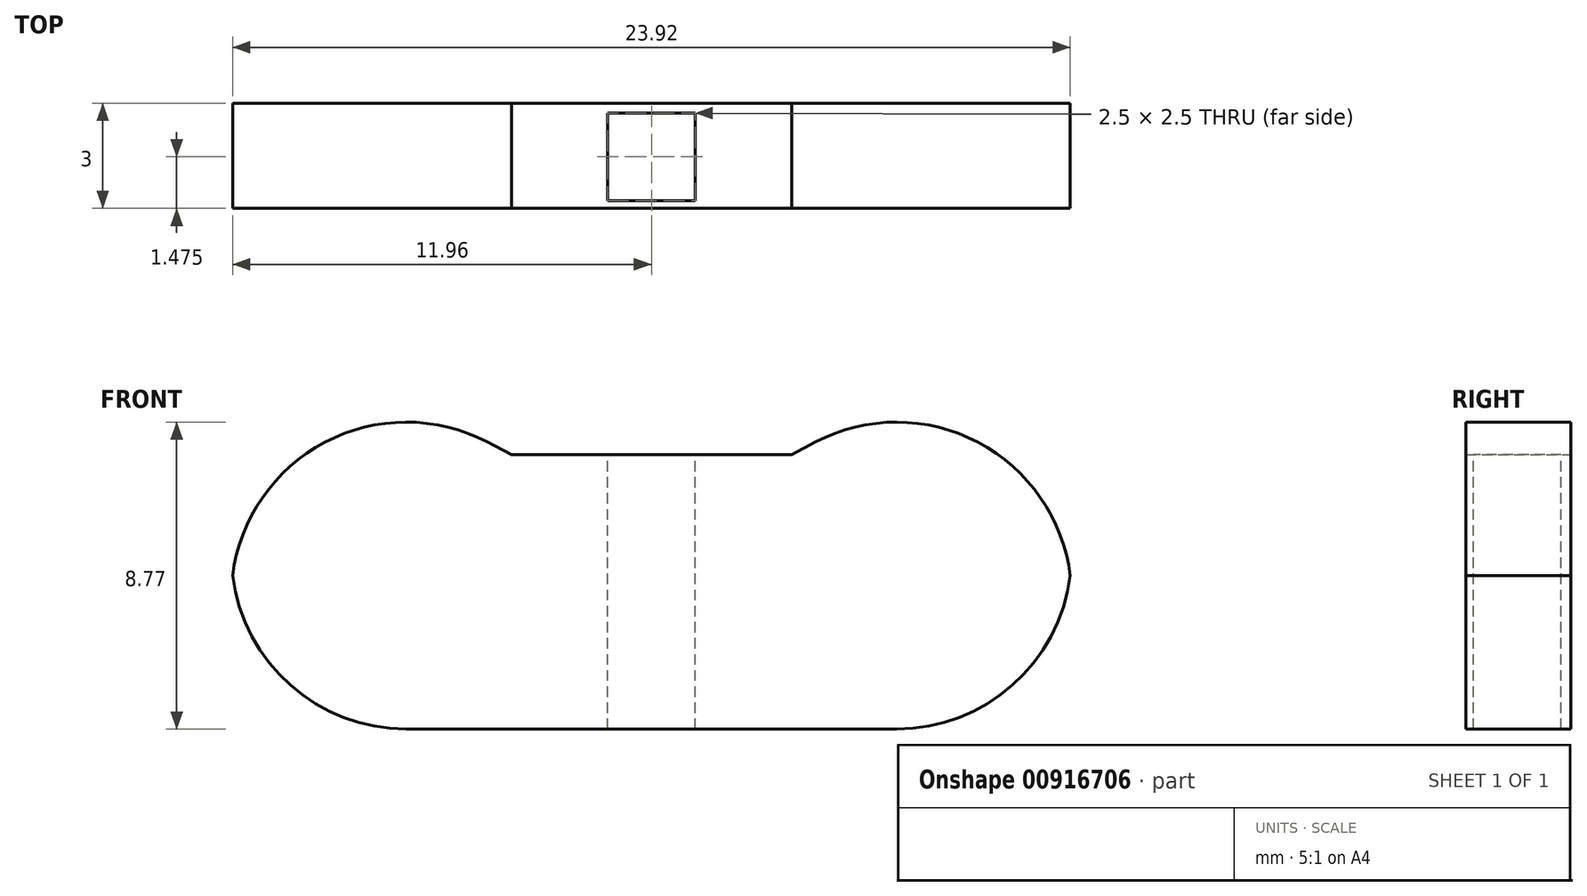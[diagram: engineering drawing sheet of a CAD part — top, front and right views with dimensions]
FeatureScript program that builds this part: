
annotation { "Feature Type Name" : "Feature", "Feature Type Description" : "" }
export const myFeature = defineFeature(function(context is Context, id is Id, definition is map)
    precondition{}
    {
        {
            var Q0;
            Q0=qCreatedBy(makeId("Front.planeOp"),FACE);
            var sketch = newSketch(context, id + "F0", { "sketchPlane" : qUnion([Q0])});
            skLineSegment(sketch, "E0", {"start": v(0, 0) * mm, "end": v(-12, 0) * mm});
            skLineSegment(sketch, "E1", {"start": v(-12, 0) * mm, "end": v(-12, 12) * mm});
            skLineSegment(sketch, "E2", {"start": v(12, 12) * mm, "end": v(12, 0) * mm});
            skLineSegment(sketch, "E3", {"start": v(12, 0) * mm, "end": v(0, 0) * mm});
            skLineSegment(sketch, "E4", {"start": v(0, 7.84) * mm, "end": v(4, 7.84) * mm});
            skLineSegment(sketch, "E5", {"start": v(4, 7.84) * mm, "end": v(0, 7.84) * mm});
            skLineSegment(sketch, "E6", {"start": v(-4, 7.84) * mm, "end": v(0, 7.84) * mm});
            skLineSegment(sketch, "E7", {"start": v(-12, 12) * mm, "end": v(-4, 7.84) * mm});
            skLineSegment(sketch, "E8", {"start": v(4, 7.84) * mm, "end": v(12, 12) * mm});
            skSolve(sketch);
        }
        {
            var Q0;
            Q0=qCreatedBy(makeId("Top.planeOp"),FACE);
            var sketch = newSketch(context, id + "F1", { "sketchPlane" : qUnion([Q0])});
            skLineSegment(sketch, "E9", {"start": v(0, 0) * mm, "end": v(0, 3) * mm});
            skSolve(sketch);
        }
        {
            var Q0;
            Q0 = qSketchRegion(id + "F0", true);
            var Q1;
            Q1 = qConstructionFilter(qBodyType(qCreatedBy(id + "F1" ,EDGE), BodyType.WIRE), ConstructionObject.NO);
            sweep(context, id + "F2", {"profiles" : qUnion([Q0]), "path" : qUnion([Q1])});
        }
        {
            var Q0;
            Q0=makeQuery(id+"F2.opSweep","SWEPT_EDGE",EDGE,{"disambiguationData":[OSD([sQuery(id+"F0.wireOp",EDGE,"RvSbD9WY-HRrn-z7GH-15Zz-RYbIcrGVxp82"),sQuery(id+"F0.wireOp",EDGE,"E2"),sQuery(id+"F1.wireOp",EDGE,"E9")])]});
            fillet(context, id + "F3", {"entities" : qUnion([Q0]), "radius" : 5 * mm, "tangentPropagation" : true, "allowEdgeOverflow" : false});
        }
        {
            var Q0;
            Q0=makeQuery(id+"F2.opSweep","SWEPT_EDGE",EDGE,{"disambiguationData":[OSD([sQuery(id+"F0.wireOp",EDGE,"E1"),sQuery(id+"F0.wireOp",EDGE,"8VaGYOir-d4IO-M7h7-wfaD-nDNDzF7UBFLd"),sQuery(id+"F1.wireOp",EDGE,"E9")])]});
            fillet(context, id + "F4", {"entities" : qUnion([Q0]), "radius" : 5 * mm, "tangentPropagation" : true, "allowEdgeOverflow" : false});
        }
        {
            var Q0;
            Q0=qCreatedBy(makeId("Top.planeOp"),FACE);
            var sketch = newSketch(context, id + "F5", { "sketchPlane" : qUnion([Q0])});
            skLineSegment(sketch, "E10.bottom", {"start": v(-1.25, 0.22) * mm, "end": v(1.25, 0.22) * mm});
            skLineSegment(sketch, "E10.top", {"start": v(-1.25, 2.72) * mm, "end": v(1.25, 2.72) * mm});
            skLineSegment(sketch, "E10.left", {"start": v(-1.25, 0.22) * mm, "end": v(-1.25, 2.72) * mm});
            skLineSegment(sketch, "E10.right", {"start": v(1.25, 0.22) * mm, "end": v(1.25, 2.72) * mm});
            skPoint(sketch, "E10.middle", {"position": v(0, 1.47) * mm});
            skSolve(sketch);
        }
        {
            var Q0;
            Q0=qCreatedBy(makeId("Front.planeOp"),FACE);
            var sketch = newSketch(context, id + "F6", { "sketchPlane" : qUnion([Q0])});
            skLineSegment(sketch, "E11", {"start": v(0, -1.3) * mm, "end": v(0, 11.7) * mm});
            skSolve(sketch);
        }
        {
            var Q0;
            Q0 = qSketchRegion(id + "F5", true);
            var Q1;
            Q1 = qConstructionFilter(qBodyType(qCreatedBy(id + "F6" ,EDGE), BodyType.WIRE), ConstructionObject.NO);
            sweep(context, id + "F7", {"operationType" : NewBodyOperationType.REMOVE, "profiles" : qUnion([Q0]), "path" : qUnion([Q1])});
        }
    });
